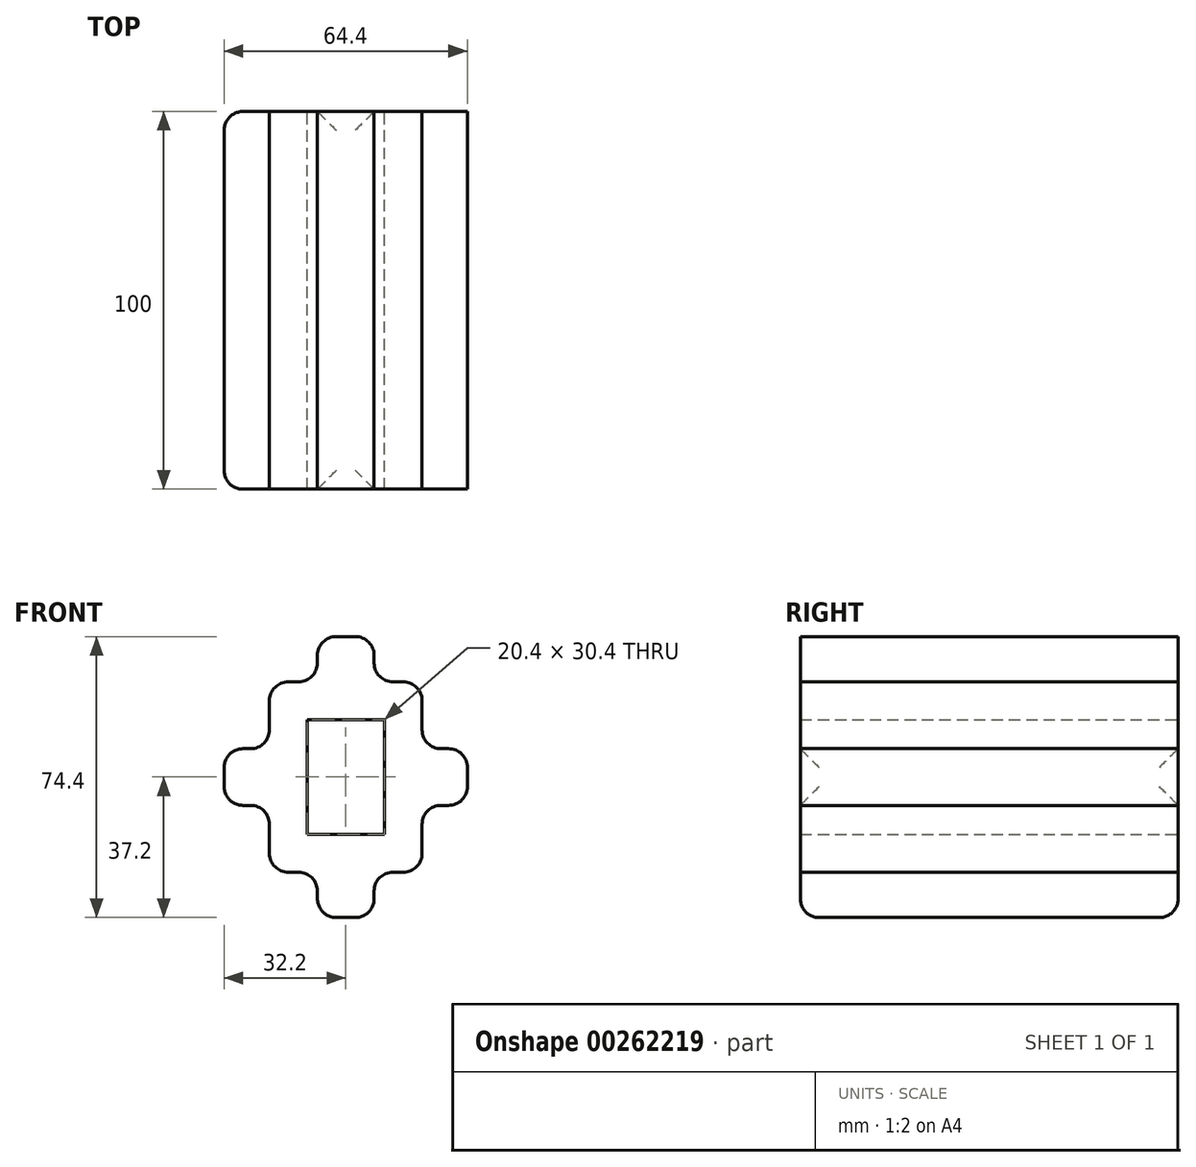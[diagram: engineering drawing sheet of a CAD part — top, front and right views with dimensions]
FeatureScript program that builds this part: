
annotation { "Feature Type Name" : "Feature", "Feature Type Description" : "" }
export const myFeature = defineFeature(function(context is Context, id is Id, definition is map)
    precondition{}
    {
        {
            var Q0;
            Q0=qCreatedBy(makeId("Front.planeOp"),FACE);
            var sketch = newSketch(context, id + "F0", { "sketchPlane" : qUnion([Q0])});
            skLineSegment(sketch, "E0.bottom", {"start": v(10.2, -15.2) * mm, "end": v(-10.2, -15.2) * mm});
            skLineSegment(sketch, "E0.top", {"start": v(10.2, 15.2) * mm, "end": v(-10.2, 15.2) * mm});
            skLineSegment(sketch, "E0.left", {"start": v(10.2, -15.2) * mm, "end": v(10.2, 15.2) * mm});
            skLineSegment(sketch, "E0.right", {"start": v(-10.2, -15.2) * mm, "end": v(-10.2, 15.2) * mm});
            skPoint(sketch, "E0.middle", {"position": v(0, 0) * mm});
            skLineSegment(sketch, "E1.bottom", {"start": v(20.2, -25.2) * mm, "end": v(-20.2, -25.2) * mm});
            skLineSegment(sketch, "E1.top", {"start": v(20.2, 25.2) * mm, "end": v(-20.2, 25.2) * mm});
            skLineSegment(sketch, "E1.left", {"start": v(20.2, -25.2) * mm, "end": v(20.2, 25.2) * mm});
            skLineSegment(sketch, "E1.right", {"start": v(-20.2, -25.2) * mm, "end": v(-20.2, 25.2) * mm});
            skLineSegment(sketch, "E2.bottom", {"start": v(32.2, -7.5) * mm, "end": v(-32.2, -7.5) * mm});
            skLineSegment(sketch, "E2.top", {"start": v(32.2, 7.5) * mm, "end": v(-32.2, 7.5) * mm});
            skLineSegment(sketch, "E2.left", {"start": v(32.2, -7.5) * mm, "end": v(32.2, 7.5) * mm});
            skLineSegment(sketch, "E2.right", {"start": v(-32.2, -7.5) * mm, "end": v(-32.2, 7.5) * mm});
            skLineSegment(sketch, "E3.bottom", {"start": v(7.5, 37.2) * mm, "end": v(-7.5, 37.2) * mm});
            skLineSegment(sketch, "E3.top", {"start": v(7.5, -37.2) * mm, "end": v(-7.5, -37.2) * mm});
            skLineSegment(sketch, "E3.left", {"start": v(7.5, 37.2) * mm, "end": v(7.5, -37.2) * mm});
            skLineSegment(sketch, "E3.right", {"start": v(-7.5, 37.2) * mm, "end": v(-7.5, -37.2) * mm});
            skLineSegment(sketch, "E4", {"start": v(-7.5, 37.2) * mm, "end": v(10.2, 15.2) * mm, "construction": true});
            skSolve(sketch);
        }
        {
            var Q0;
            Q0 = qSketchRegion(id + "F0", true);
            extrude(context, id + "F1", {"entities" : qUnion([Q0]), "depth" : 100 * mm, "offsetDistance" : 25 * mm});
        }
        {
            var Q0;
            Q0=makeQuery(id+"F1.opExtrude","SWEPT_EDGE",EDGE,{"disambiguationData":[OSD([sQuery(id+"F0.wireOp",EDGE,"E1.top"),sQuery(id+"F0.wireOp",EDGE,"E1.right")])]});
            var Q1;
            Q1=makeQuery(id+"F1.opExtrude","SWEPT_EDGE",EDGE,{"disambiguationData":[OSD([sQuery(id+"F0.wireOp",EDGE,"E1.top"),sQuery(id+"F0.wireOp",EDGE,"E1.left")])]});
            var Q2;
            Q2=makeQuery(id+"F1.opExtrude","SWEPT_EDGE",EDGE,{"disambiguationData":[OSD([sQuery(id+"F0.wireOp",EDGE,"E1.bottom"),sQuery(id+"F0.wireOp",EDGE,"E1.left")])]});
            var Q3;
            Q3=makeQuery(id+"F1.opExtrude","SWEPT_EDGE",EDGE,{"disambiguationData":[OSD([sQuery(id+"F0.wireOp",EDGE,"E1.bottom"),sQuery(id+"F0.wireOp",EDGE,"E1.right")])]});
            var Q4;
            Q4=makeQuery(id+"F1.opExtrude","SWEPT_EDGE",EDGE,{"disambiguationData":[OSD([sQuery(id+"F0.wireOp",EDGE,"E2.top"),sQuery(id+"F0.wireOp",EDGE,"E2.left")])]});
            var Q5;
            Q5=makeQuery(id+"F1.opExtrude","SWEPT_EDGE",EDGE,{"disambiguationData":[OSD([sQuery(id+"F0.wireOp",EDGE,"E2.bottom"),sQuery(id+"F0.wireOp",EDGE,"E2.left")])]});
            var Q6;
            Q6=makeQuery(id+"F1.opExtrude","SWEPT_EDGE",EDGE,{"disambiguationData":[OSD([sQuery(id+"F0.wireOp",EDGE,"E1.left"),sQuery(id+"F0.wireOp",EDGE,"E2.top")])]});
            var Q7;
            Q7=makeQuery(id+"F1.opExtrude","SWEPT_EDGE",EDGE,{"disambiguationData":[OSD([sQuery(id+"F0.wireOp",EDGE,"E1.left"),sQuery(id+"F0.wireOp",EDGE,"E2.bottom")])]});
            var Q8;
            Q8=makeQuery(id+"F1.opExtrude","SWEPT_EDGE",EDGE,{"disambiguationData":[OSD([sQuery(id+"F0.wireOp",EDGE,"E1.top"),sQuery(id+"F0.wireOp",EDGE,"E3.left")])]});
            var Q9;
            Q9=makeQuery(id+"F1.opExtrude","SWEPT_EDGE",EDGE,{"disambiguationData":[OSD([sQuery(id+"F0.wireOp",EDGE,"E3.bottom"),sQuery(id+"F0.wireOp",EDGE,"E3.left")])]});
            var Q10;
            Q10=makeQuery(id+"F1.opExtrude","SWEPT_EDGE",EDGE,{"disambiguationData":[OSD([sQuery(id+"F0.wireOp",EDGE,"E3.bottom"),sQuery(id+"F0.wireOp",EDGE,"E3.right")])]});
            var Q11;
            Q11=makeQuery(id+"F1.opExtrude","SWEPT_EDGE",EDGE,{"disambiguationData":[OSD([sQuery(id+"F0.wireOp",EDGE,"E1.top"),sQuery(id+"F0.wireOp",EDGE,"E3.right")])]});
            var Q12;
            Q12=makeQuery(id+"F1.opExtrude","SWEPT_EDGE",EDGE,{"disambiguationData":[OSD([sQuery(id+"F0.wireOp",EDGE,"E1.right"),sQuery(id+"F0.wireOp",EDGE,"E2.top")])]});
            var Q13;
            Q13=makeQuery(id+"F1.opExtrude","SWEPT_FACE",FACE,{"disambiguationData":[OSD([sQuery(id+"F0.wireOp",EDGE,"E2.right")])]});
            var Q14;
            Q14=makeQuery(id+"F1.opExtrude","SWEPT_EDGE",EDGE,{"disambiguationData":[OSD([sQuery(id+"F0.wireOp",EDGE,"E1.right"),sQuery(id+"F0.wireOp",EDGE,"E2.bottom")])]});
            var Q15;
            Q15=makeQuery(id+"F1.opExtrude","SWEPT_EDGE",EDGE,{"disambiguationData":[OSD([sQuery(id+"F0.wireOp",EDGE,"E1.bottom"),sQuery(id+"F0.wireOp",EDGE,"E3.right")])]});
            var Q16;
            Q16=makeQuery(id+"F1.opExtrude","SWEPT_EDGE",EDGE,{"disambiguationData":[OSD([sQuery(id+"F0.wireOp",EDGE,"E3.top"),sQuery(id+"F0.wireOp",EDGE,"E3.right")])]});
            var Q17;
            Q17=makeQuery(id+"F1.opExtrude","SWEPT_FACE",FACE,{"disambiguationData":[OSD([sQuery(id+"F0.wireOp",EDGE,"E3.top")])]});
            var Q18;
            Q18=makeQuery(id+"F1.opExtrude","SWEPT_EDGE",EDGE,{"disambiguationData":[OSD([sQuery(id+"F0.wireOp",EDGE,"E1.bottom"),sQuery(id+"F0.wireOp",EDGE,"E3.left")])]});
            fillet(context, id + "F2", {"entities" : qUnion([Q0, Q1, Q2, Q3, Q4, Q5, Q6, Q7, Q8, Q9, Q10, Q11, Q12, Q13, Q14, Q15, Q16, Q17, Q18]), "radius" : 5 * mm, "tangentPropagation" : true, "allowEdgeOverflow" : false});
        }
    });
